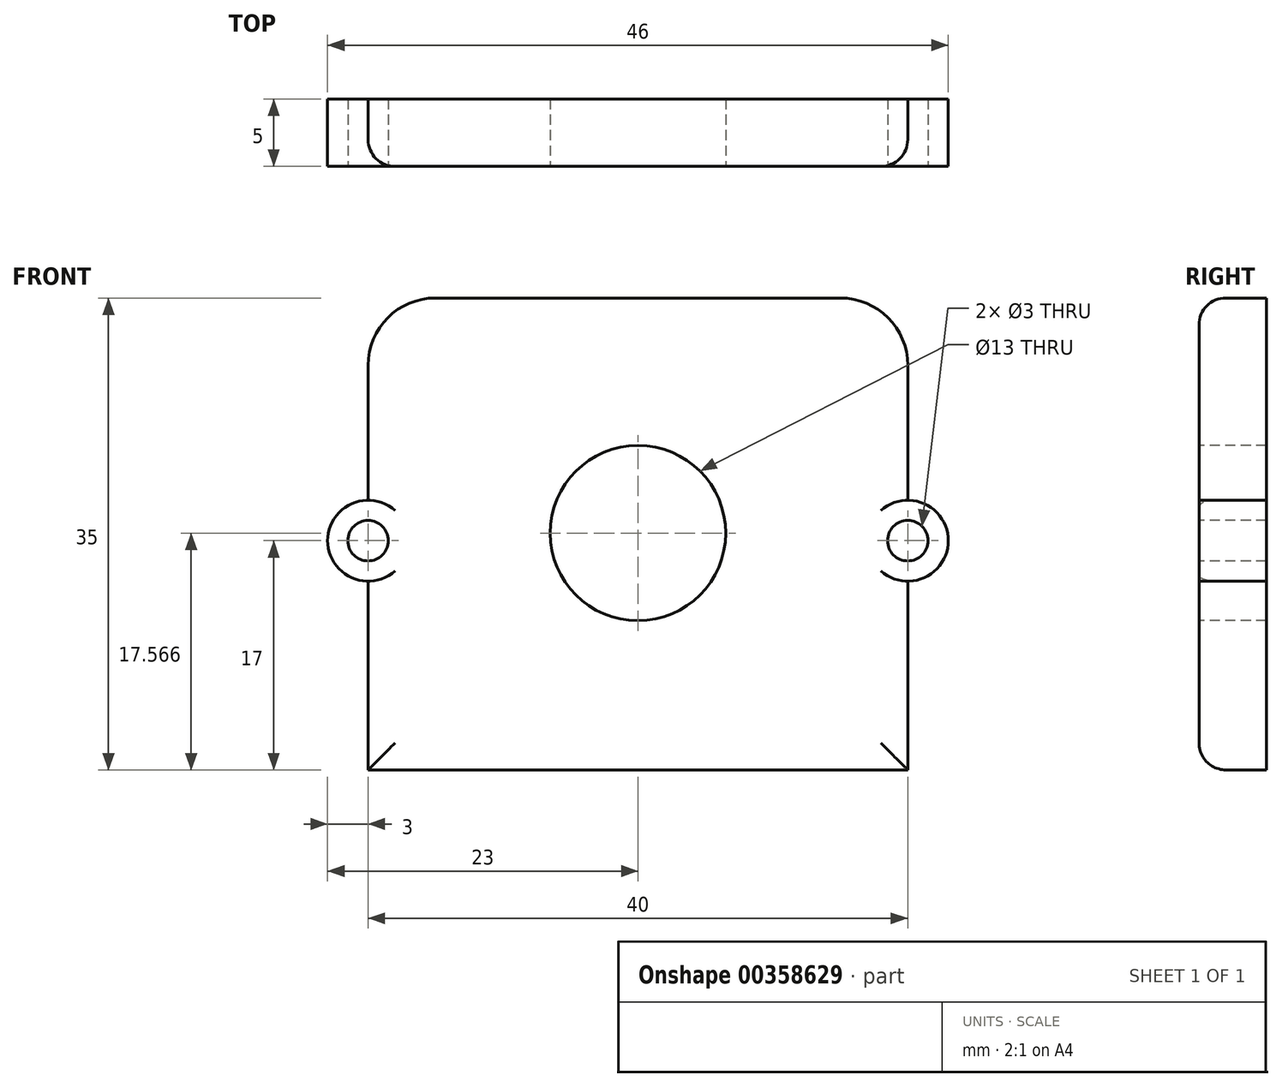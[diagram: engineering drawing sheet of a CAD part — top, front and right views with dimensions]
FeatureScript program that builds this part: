
annotation { "Feature Type Name" : "Feature", "Feature Type Description" : "" }
export const myFeature = defineFeature(function(context is Context, id is Id, definition is map)
    precondition{}
    {
        {
            var Q0;
            Q0=qCreatedBy(makeId("Front.planeOp"),FACE);
            var sketch = newSketch(context, id + "F0", { "sketchPlane" : qUnion([Q0])});
            skLineSegment(sketch, "E0.bottom", {"start": v(0, 0) * mm, "end": v(40, 0) * mm});
            skLineSegment(sketch, "E0.top", {"start": v(5, 35) * mm, "end": v(35, 35) * mm});
            skLineSegment(sketch, "E0.left", {"start": v(0, 0) * mm, "end": v(0, 14) * mm});
            skLineSegment(sketch, "E0.right", {"start": v(40, 0) * mm, "end": v(40, 14) * mm});
            skArc(sketch, "E1", {"start": v(0, 20) * mm, "mid": v(-3, 17) * mm, "end": v(0, 14) * mm});
            skArc(sketch, "E2", {"start": v(40, 14) * mm, "mid": v(43, 17) * mm, "end": v(40, 20) * mm});
            skPoint(sketch, "E3.visualSharp", {"position": v(0, 35) * mm});
            skArc(sketch, "E3.filletArc", {"start": v(5, 35) * mm, "mid": v(1.46, 33.54) * mm, "end": v(0, 30) * mm});
            skPoint(sketch, "E4.visualSharp", {"position": v(40, 35) * mm});
            skArc(sketch, "E4.filletArc", {"start": v(40, 30) * mm, "mid": v(38.54, 33.54) * mm, "end": v(35, 35) * mm});
            skLineSegment(sketch, "E5.trimOffspring", {"start": v(0, 20) * mm, "end": v(0, 30) * mm});
            skLineSegment(sketch, "E6.trimOffspring", {"start": v(40, 20) * mm, "end": v(40, 30) * mm});
            skSolve(sketch);
        }
        {
            var Q0;
            Q0=makeQuery(id+"F0.imprint","IMPRINT",FACE,{"disambiguationData":[TD([[makeQuery(id+"F0.imprint","IMPRINT",EDGE,{"derivedFrom":sQuery(id+"F0.wireOp",EDGE,"E0.bottom")}),1.0]])]});
            extrude(context, id + "F1", {"entities" : qUnion([Q0]), "depth" : 5 * mm});
        }
        {
            var Q0;
            Q0=makeQuery(id+"F1.opExtrude","CAP_FACE",FACE,{"disambiguationData":[OSD([sQuery(id+"F0.wireOp",EDGE,"E0.bottom"),sQuery(id+"F0.wireOp",EDGE,"E0.top"),sQuery(id+"F0.wireOp",EDGE,"E0.left"),sQuery(id+"F0.wireOp",EDGE,"E0.right"),sQuery(id+"F0.wireOp",EDGE,"E1"),sQuery(id+"F0.wireOp",EDGE,"E2"),sQuery(id+"F0.wireOp",EDGE,"E3.filletArc"),sQuery(id+"F0.wireOp",EDGE,"E4.filletArc"),sQuery(id+"F0.wireOp",EDGE,"E5.trimOffspring"),sQuery(id+"F0.wireOp",EDGE,"E6.trimOffspring")])],"isStart":false});
            var sketch = newSketch(context, id + "F2", { "sketchPlane" : qUnion([Q0])});
            skCircle(sketch, "E7", {"center": v(0, 17) * mm, "radius": 1.5 * mm});
            skCircle(sketch, "E8", {"center": v(40, 17) * mm, "radius": 1.5 * mm});
            skSolve(sketch);
        }
        {
            var Q0;
            Q0=makeQuery(id+"F2.imprint","IMPRINT",FACE,{"disambiguationData":[TD([[makeQuery(id+"F2.imprint","IMPRINT",EDGE,{"derivedFrom":sQuery(id+"F2.wireOp",EDGE,"E7")}),1.0]])]});
            var Q1;
            Q1=makeQuery(id+"F2.imprint","IMPRINT",FACE,{"disambiguationData":[TD([[makeQuery(id+"F2.imprint","IMPRINT",EDGE,{"derivedFrom":sQuery(id+"F2.wireOp",EDGE,"E8")}),1.0]])]});
            extrude(context, id + "F3", {"entities" : qUnion([Q0, Q1]), "operationType" : NewBodyOperationType.REMOVE, "oppositeDirection" : true, "depth" : 25 * mm});
        }
        {
            var Q0;
            Q0=makeQuery(id+"F1.opExtrude","CAP_FACE",FACE,{"disambiguationData":[OSD([sQuery(id+"F0.wireOp",EDGE,"E0.bottom"),sQuery(id+"F0.wireOp",EDGE,"E0.top"),sQuery(id+"F0.wireOp",EDGE,"E0.left"),sQuery(id+"F0.wireOp",EDGE,"E0.right"),sQuery(id+"F0.wireOp",EDGE,"E1"),sQuery(id+"F0.wireOp",EDGE,"E2"),sQuery(id+"F0.wireOp",EDGE,"E3.filletArc"),sQuery(id+"F0.wireOp",EDGE,"E4.filletArc"),sQuery(id+"F0.wireOp",EDGE,"E5.trimOffspring"),sQuery(id+"F0.wireOp",EDGE,"E6.trimOffspring")])],"isStart":false});
            var sketch = newSketch(context, id + "F4", { "sketchPlane" : qUnion([Q0])});
            skCircle(sketch, "E9", {"center": v(20, 17.57) * mm, "radius": 6.5 * mm});
            skPoint(sketch, "E9.centerSnap0", {"position": v(20, 35) * mm});
            skSolve(sketch);
        }
        {
            var Q0;
            Q0 = qSketchRegion(id + "F4", true);
            extrude(context, id + "F5", {"entities" : qUnion([Q0]), "operationType" : NewBodyOperationType.REMOVE, "oppositeDirection" : true, "depth" : 25 * mm});
        }
        {
            var Q0;
            Q0=makeQuery(id+"F1.opExtrude","CAP_EDGE",EDGE,{"disambiguationData":[OSD([sQuery(id+"F0.wireOp",EDGE,"E5.trimOffspring")])],"isStart":false});
            var Q1;
            Q1=makeQuery(id+"F1.opExtrude","CAP_EDGE",EDGE,{"disambiguationData":[OSD([sQuery(id+"F0.wireOp",EDGE,"E3.filletArc")])],"isStart":false});
            var Q2;
            Q2=makeQuery(id+"F1.opExtrude","CAP_EDGE",EDGE,{"disambiguationData":[OSD([sQuery(id+"F0.wireOp",EDGE,"E0.right")])],"isStart":false});
            var Q3;
            Q3=makeQuery(id+"F1.opExtrude","CAP_EDGE",EDGE,{"disambiguationData":[OSD([sQuery(id+"F0.wireOp",EDGE,"E0.bottom")])],"isStart":false});
            var Q4;
            Q4=makeQuery(id+"F1.opExtrude","CAP_EDGE",EDGE,{"disambiguationData":[OSD([sQuery(id+"F0.wireOp",EDGE,"E0.left")])],"isStart":false});
            fillet(context, id + "F6", {"entities" : qUnion([Q0, Q1, Q2, Q3, Q4]), "radius" : 2 * mm, "tangentPropagation" : true, "allowEdgeOverflow" : false});
        }
    });
